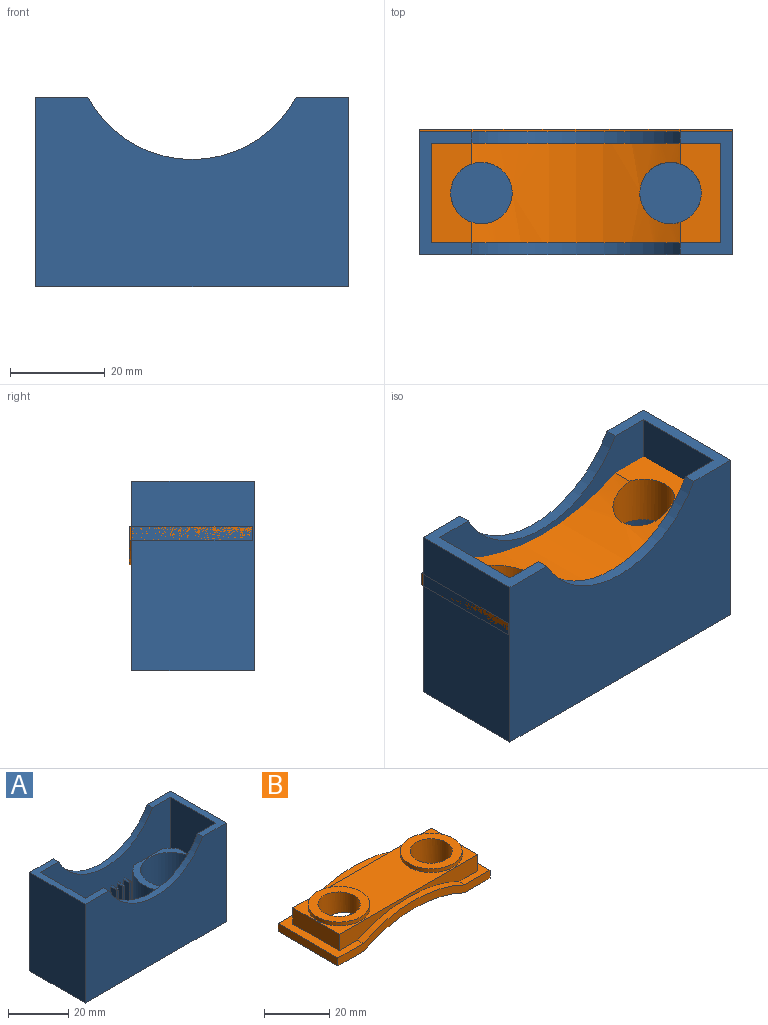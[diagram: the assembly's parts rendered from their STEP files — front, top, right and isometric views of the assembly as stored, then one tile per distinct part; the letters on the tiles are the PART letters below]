
ASSEMBLY  parts=2 mates=2
PART A: 147 faces, bbox 66x26x40 mm
  f0: cylinder r=12.5mm len=21mm, axis (0,0,-1), area 448.8mm2, adj f6,f12,f19,f141
  f1: cylinder r=12.5mm len=18mm, axis (0,0,-1), area 95.3mm2, adj f14,f19,f23,f141
  f2: cylinder r=12.5mm len=18mm, axis (0,0,-1), area 95.3mm2, adj f12,f14,f24,f141
  f3: cylinder r=12.5mm len=18mm, axis (0,0,-1), area 95.3mm2, adj f12,f18,f26,f142
  f4: cylinder r=12.5mm len=18mm, axis (0,0,-1), area 95.3mm2, adj f18,f19,f25,f142
  f5: cylinder r=12.5mm len=21mm, axis (0,0,-1), area 448.8mm2, adj f11,f12,f19,f142
  f6: plane 21x6.72mm, normal (0,0,1), area 51mm2, adj f0,f12,f19,f37,f39,f40,f41,f42
  f7: plane 21x2mm, normal (0,0,1), area 42mm2, adj f12,f19,f35,f38
  f8: plane 21x2mm, normal (0,0,1), area 42mm2, adj f12,f19,f32,f33
  f9: plane 21x2mm, normal (0,0,1), area 42mm2, adj f12,f19,f29,f31
  f10: plane 21x2mm, normal (0,0,1), area 42mm2, adj f12,f19,f30,f36
  f11: plane 21x6.72mm, normal (0,0,1), area 51mm2, adj f5,f12,f19,f34,f43,f44,f45,f46
  f12: plane 61x37mm, normal (0,1,0), area 1254.2mm2, adj f0,f2,f3,f5,f6,f7,f8,f9
  f13: plane 26x11mm, normal (0,0,1), area 107.5mm2, adj f12,f15,f16,f17,f18,f19,f27,f28
  f14: plane 37x21mm, normal (1,0,0), area 532.8mm2, adj f1,f2,f12,f19,f21,f23,f24,f141
  f15: plane 66x40mm, normal (0,-1,0), area 2228.8mm2, adj f13,f16,f20,f21,f22,f28
  f16: plane 40x26mm, normal (1,0,0), area 1040mm2, adj f13,f15,f17,f22
  f17: plane 66x40mm, normal (0,1,0), area 2228.8mm2, adj f13,f16,f20,f21,f22,f27
  f18: plane 37x21mm, normal (-1,0,0), area 532.8mm2, adj f3,f4,f12,f13,f19,f25,f26,f142
  f19: plane 61x37mm, normal (0,-1,0), area 1254.2mm2, adj f0,f1,f4,f5,f6,f7,f8,f9
  f20: plane 40x26mm, normal (-1,0,0), area 1040mm2, adj f15,f17,f21,f22
  f21: plane 26x11mm, normal (0,0,1), area 107.5mm2, adj f12,f14,f15,f17,f19,f20,f27,f28
  f22: plane 66x26mm, normal (0,0,-1), area 1716mm2, adj f15,f16,f17,f20
  f23: plane 3.72x3.72mm, normal (0,0,1), area 5.9mm2, adj f1,f14,f19
  f24: plane 3.72x3.72mm, normal (0,0,1), area 5.9mm2, adj f2,f12,f14
  f25: plane 3.72x3.72mm, normal (0,0,1), area 5.9mm2, adj f4,f18,f19
  f26: plane 3.72x3.72mm, normal (0,0,1), area 5.9mm2, adj f3,f12,f18
  f27: cylinder r=25mm len=44mm, axis (0,-1,0), area 134.5mm2, adj f13,f17,f19,f21
  f28: cylinder r=25mm len=44mm, axis (0,-1,0), area 134.5mm2, adj f12,f13,f15,f21
  f29: plane 21x14.5mm, normal (1,0,0), area 144.5mm2, adj f9,f12,f19,f63,f65,f66,f98,f127
  f30: plane 21x14.5mm, normal (-1,0,0), area 144.5mm2, adj f10,f12,f19,f64,f67,f68,f97,f125
  f31: plane 21x14.5mm, normal (-1,0,0), area 144.5mm2, adj f9,f12,f19,f57,f58,f60,f93,f121
  f32: plane 21x14.5mm, normal (1,0,0), area 144.5mm2, adj f8,f12,f19,f59,f61,f62,f94,f123
  f33: plane 21x14.5mm, normal (-1,0,0), area 144.5mm2, adj f8,f12,f19,f51,f52,f54,f89,f117
  f34: plane 21x14.5mm, normal (1,0,0), area 144.5mm2, adj f11,f12,f19,f53,f55,f56,f90,f119
  f35: plane 21x14.5mm, normal (-1,0,0), area 144.5mm2, adj f7,f12,f19,f69,f70,f72,f101,f138
  f36: plane 21x14.5mm, normal (1,0,0), area 144.5mm2, adj f10,f12,f19,f71,f73,f74,f102,f137
  f37: plane 21x14.5mm, normal (-1,0,0), area 144.5mm2, adj f6,f12,f19,f76,f79,f80,f105,f134
  f38: plane 21x14.5mm, normal (1,0,0), area 144.5mm2, adj f7,f12,f19,f75,f77,f78,f106,f133
  f39: plane 14.5x2.5mm, normal (1,0,0), area 36.3mm2, adj f6,f19,f84,f129
  f40: plane 14.5x2.5mm, normal (-1,0,0), area 36.3mm2, adj f6,f19,f83,f130
  f41: plane 14.5x2.5mm, normal (-1,0,0), area 36.3mm2, adj f6,f12,f48,f109
  f42: plane 14.5x2.5mm, normal (1,0,0), area 36.3mm2, adj f6,f12,f47,f110
  f43: plane 14.5x2.5mm, normal (-1,0,0), area 36.3mm2, adj f11,f19,f81,f113
  f44: plane 14.5x2.5mm, normal (1,0,0), area 36.3mm2, adj f11,f19,f82,f115
  f45: plane 14.5x2.5mm, normal (-1,0,0), area 36.3mm2, adj f11,f12,f50,f85
  f46: plane 14.5x2.5mm, normal (1,0,0), area 36.3mm2, adj f11,f12,f49,f86
  f47: plane 14.5x0.5mm, normal (0.71,0.71,0), area 10.3mm2, adj f6,f42,f48,f112
  f48: plane 14.5x0.5mm, normal (-0.71,0.71,0), area 10.3mm2, adj f6,f41,f47,f111
  f49: plane 14.5x0.5mm, normal (0.71,0.71,0), area 10.3mm2, adj f11,f46,f50,f88
  f50: plane 14.5x0.5mm, normal (-0.71,0.71,0), area 10.3mm2, adj f11,f45,f49,f87
  f51: plane 10x0.5mm, normal (-0.71,-0.71,0), area 6.9mm2, adj f33,f52,f53,f118
  f52: plane 16x0.5mm, normal (-0.71,0,0.71), area 11mm2, adj f33,f51,f54,f55
  f53: plane 10x0.5mm, normal (0.71,-0.71,0), area 6.9mm2, adj f34,f51,f55,f120
  f54: plane 10x0.5mm, normal (-0.71,0.71,0), area 6.9mm2, adj f33,f52,f56,f91
  f55: plane 16x0.5mm, normal (0.71,0,0.71), area 11mm2, adj f34,f52,f53,f56
  f56: plane 10x0.5mm, normal (0.71,0.71,0), area 6.9mm2, adj f34,f54,f55,f92
  f57: plane 10x0.5mm, normal (-0.71,-0.71,0), area 6.9mm2, adj f31,f58,f59,f122
  f58: plane 16x0.5mm, normal (-0.71,0,0.71), area 11mm2, adj f31,f57,f60,f61
  f59: plane 10x0.5mm, normal (0.71,-0.71,0), area 6.9mm2, adj f32,f57,f61,f124
  f60: plane 10x0.5mm, normal (-0.71,0.71,0), area 6.9mm2, adj f31,f58,f62,f95
  f61: plane 16x0.5mm, normal (0.71,0,0.71), area 11mm2, adj f32,f58,f59,f62
  f62: plane 10x0.5mm, normal (0.71,0.71,0), area 6.9mm2, adj f32,f60,f61,f96
  f63: plane 10x0.5mm, normal (0.71,-0.71,0), area 6.9mm2, adj f29,f64,f65,f128
  f64: plane 10x0.5mm, normal (-0.71,-0.71,0), area 6.9mm2, adj f30,f63,f67,f126
  f65: plane 16x0.5mm, normal (0.71,0,0.71), area 11mm2, adj f29,f63,f66,f67
  f66: plane 10x0.5mm, normal (0.71,0.71,0), area 6.9mm2, adj f29,f65,f68,f100
  f67: plane 16x0.5mm, normal (-0.71,0,0.71), area 11mm2, adj f30,f64,f65,f68
  f68: plane 10x0.5mm, normal (-0.71,0.71,0), area 6.9mm2, adj f30,f66,f67,f99
  f69: plane 10x0.5mm, normal (-0.71,-0.71,0), area 6.9mm2, adj f35,f70,f71,f140
  f70: plane 16x0.5mm, normal (-0.71,0,0.71), area 11mm2, adj f35,f69,f72,f73
  f71: plane 10x0.5mm, normal (0.71,-0.71,0), area 6.9mm2, adj f36,f69,f73,f139
  f72: plane 10x0.5mm, normal (-0.71,0.71,0), area 6.9mm2, adj f35,f70,f74,f103
  f73: plane 16x0.5mm, normal (0.71,0,0.71), area 11mm2, adj f36,f70,f71,f74
  f74: plane 10x0.5mm, normal (0.71,0.71,0), area 6.9mm2, adj f36,f72,f73,f104
  f75: plane 10x0.5mm, normal (0.71,-0.71,0), area 6.9mm2, adj f38,f76,f77,f135
  f76: plane 10x0.5mm, normal (-0.71,-0.71,0), area 6.9mm2, adj f37,f75,f79,f136
  f77: plane 16x0.5mm, normal (0.71,0,0.71), area 11mm2, adj f38,f75,f78,f79
  f78: plane 10x0.5mm, normal (0.71,0.71,0), area 6.9mm2, adj f38,f77,f80,f108
  f79: plane 16x0.5mm, normal (-0.71,0,0.71), area 11mm2, adj f37,f76,f77,f80
  f80: plane 10x0.5mm, normal (-0.71,0.71,0), area 6.9mm2, adj f37,f78,f79,f107
  f81: plane 14.5x0.5mm, normal (-0.71,-0.71,0), area 10.3mm2, adj f11,f43,f82,f114
  f82: plane 14.5x0.5mm, normal (0.71,-0.71,0), area 10.3mm2, adj f11,f44,f81,f116
  f83: plane 14.5x0.5mm, normal (-0.71,-0.71,0), area 10.3mm2, adj f6,f40,f84,f132
  f84: plane 14.5x0.5mm, normal (0.71,-0.71,0), area 10.3mm2, adj f6,f39,f83,f131
  f85: plane 2.5x0.5mm, normal (-0.71,0,0.71), area 1.7mm2, adj f12,f45,f86,f87
  f86: plane 2.5x0.5mm, normal (0.71,0,0.71), area 1.7mm2, adj f12,f46,f85,f88
  f87: plane 0.71x0.5mm, normal (-0.5,0.5,0.71), area 0.2mm2, adj f50,f85,f88
  f88: plane 0.71x0.5mm, normal (0.5,0.5,0.71), area 0.3mm2, adj f49,f86,f87
  f89: plane 2.5x0.5mm, normal (-0.71,0,0.71), area 1.7mm2, adj f12,f33,f90,f91
  f90: plane 2.5x0.5mm, normal (0.71,0,0.71), area 1.7mm2, adj f12,f34,f89,f92
  f91: plane 0.71x0.5mm, normal (-0.5,0.5,0.71), area 0.2mm2, adj f54,f89,f92
  f92: plane 0.71x0.5mm, normal (0.5,0.5,0.71), area 0.2mm2, adj f56,f90,f91
  f93: plane 2.5x0.5mm, normal (-0.71,0,0.71), area 1.7mm2, adj f12,f31,f94,f95
  f94: plane 2.5x0.5mm, normal (0.71,0,0.71), area 1.7mm2, adj f12,f32,f93,f96
  f95: plane 0.71x0.5mm, normal (-0.5,0.5,0.71), area 0.2mm2, adj f60,f93,f96
  f96: plane 0.71x0.5mm, normal (0.5,0.5,0.71), area 0.2mm2, adj f62,f94,f95
  f97: plane 2.5x0.5mm, normal (-0.71,0,0.71), area 1.7mm2, adj f12,f30,f98,f99
  f98: plane 2.5x0.5mm, normal (0.71,0,0.71), area 1.7mm2, adj f12,f29,f97,f100
  f99: plane 0.71x0.5mm, normal (-0.5,0.5,0.71), area 0.2mm2, adj f68,f97,f100
  f100: plane 0.71x0.5mm, normal (0.5,0.5,0.71), area 0.2mm2, adj f66,f98,f99
  f101: plane 2.5x0.5mm, normal (-0.71,0,0.71), area 1.7mm2, adj f12,f35,f102,f103
  f102: plane 2.5x0.5mm, normal (0.71,0,0.71), area 1.7mm2, adj f12,f36,f101,f104
  f103: plane 0.71x0.5mm, normal (-0.5,0.5,0.71), area 0.3mm2, adj f72,f101,f104
  f104: plane 0.71x0.5mm, normal (0.5,0.5,0.71), area 0.2mm2, adj f74,f102,f103
  f105: plane 2.5x0.5mm, normal (-0.71,0,0.71), area 1.7mm2, adj f12,f37,f106,f107
  f106: plane 2.5x0.5mm, normal (0.71,0,0.71), area 1.7mm2, adj f12,f38,f105,f108
  f107: plane 0.71x0.5mm, normal (-0.5,0.5,0.71), area 0.2mm2, adj f80,f105,f108
  f108: plane 0.71x0.5mm, normal (0.5,0.5,0.71), area 0.2mm2, adj f78,f106,f107
  f109: plane 2.5x0.5mm, normal (-0.71,0,0.71), area 1.7mm2, adj f12,f41,f110,f111
  f110: plane 2.5x0.5mm, normal (0.71,0,0.71), area 1.7mm2, adj f12,f42,f109,f112
  f111: plane 0.71x0.5mm, normal (-0.5,0.5,0.71), area 0.2mm2, adj f48,f109,f112
  f112: plane 0.71x0.5mm, normal (0.5,0.5,0.71), area 0.3mm2, adj f47,f110,f111
  f113: plane 2.5x0.5mm, normal (-0.71,0,0.71), area 1.7mm2, adj f19,f43,f114,f115
  f114: plane 0.71x0.5mm, normal (-0.5,-0.5,0.71), area 0.2mm2, adj f81,f113,f116
  f115: plane 2.5x0.5mm, normal (0.71,0,0.71), area 1.7mm2, adj f19,f44,f113,f116
  f116: plane 0.71x0.5mm, normal (0.5,-0.5,0.71), area 0.3mm2, adj f82,f114,f115
  f117: plane 2.5x0.5mm, normal (-0.71,0,0.71), area 1.7mm2, adj f19,f33,f118,f119
  f118: plane 0.71x0.5mm, normal (-0.5,-0.5,0.71), area 0.2mm2, adj f51,f117,f120
  f119: plane 2.5x0.5mm, normal (0.71,0,0.71), area 1.7mm2, adj f19,f34,f117,f120
  f120: plane 0.71x0.5mm, normal (0.5,-0.5,0.71), area 0.3mm2, adj f53,f118,f119
  f121: plane 2.5x0.5mm, normal (-0.71,0,0.71), area 1.7mm2, adj f19,f31,f122,f123
  f122: plane 0.71x0.5mm, normal (-0.5,-0.5,0.71), area 0.2mm2, adj f57,f121,f124
  f123: plane 2.5x0.5mm, normal (0.71,0,0.71), area 1.7mm2, adj f19,f32,f121,f124
  f124: plane 0.71x0.5mm, normal (0.5,-0.5,0.71), area 0.2mm2, adj f59,f122,f123
  f125: plane 2.5x0.5mm, normal (-0.71,0,0.71), area 1.7mm2, adj f19,f30,f126,f127
  f126: plane 0.71x0.5mm, normal (-0.5,-0.5,0.71), area 0.2mm2, adj f64,f125,f128
  f127: plane 2.5x0.5mm, normal (0.71,0,0.71), area 1.7mm2, adj f19,f29,f125,f128
  f128: plane 0.71x0.5mm, normal (0.5,-0.5,0.71), area 0.3mm2, adj f63,f126,f127
  f129: plane 2.5x0.5mm, normal (0.71,0,0.71), area 1.7mm2, adj f19,f39,f130,f131
  f130: plane 2.5x0.5mm, normal (-0.71,0,0.71), area 1.7mm2, adj f19,f40,f129,f132
  f131: plane 0.71x0.5mm, normal (0.5,-0.5,0.71), area 0.3mm2, adj f84,f129,f132
  f132: plane 0.71x0.5mm, normal (-0.5,-0.5,0.71), area 0.2mm2, adj f83,f130,f131
  f133: plane 2.5x0.5mm, normal (0.71,0,0.71), area 1.7mm2, adj f19,f38,f134,f135
  f134: plane 2.5x0.5mm, normal (-0.71,0,0.71), area 1.7mm2, adj f19,f37,f133,f136
  f135: plane 0.71x0.5mm, normal (0.5,-0.5,0.71), area 0.3mm2, adj f75,f133,f136
  f136: plane 0.71x0.5mm, normal (-0.5,-0.5,0.71), area 0.2mm2, adj f76,f134,f135
  f137: plane 2.5x0.5mm, normal (0.71,0,0.71), area 1.7mm2, adj f19,f36,f138,f139
  f138: plane 2.5x0.5mm, normal (-0.71,0,0.71), area 1.7mm2, adj f19,f35,f137,f140
  f139: plane 0.71x0.5mm, normal (0.5,-0.5,0.71), area 0.2mm2, adj f71,f137,f140
  f140: plane 0.71x0.5mm, normal (-0.5,-0.5,0.71), area 0.2mm2, adj f69,f138,f139
  f141: plane 23x21mm, normal (0,0,1), area 121.5mm2, adj f0,f1,f2,f12,f14,f19,f144
  f142: plane 23x21mm, normal (0,0,1), area 121.5mm2, adj f3,f4,f5,f12,f18,f19,f146
  f143: plane 20x20mm, normal (0,0,1), area 314.2mm2, adj f144
  f144: cylinder r=10mm len=20mm, axis (0,0,-1), area 1131mm2, adj f141,f143
  f145: plane 20x20mm, normal (0,0,1), area 314.2mm2, adj f146
  f146: cylinder r=10mm len=20mm, axis (0,0,-1), area 1131mm2, adj f142,f145
PART B: 22 faces, bbox 66x26x10.5 mm
  f0: plane 60x6.1mm, normal (0,-1,0), area 214.8mm2, adj f1,f3,f4,f11,f12,f15
  f1: plane 20x6.1mm, normal (1,0,0), area 122mm2, adj f0,f2,f4,f12
  f2: plane 60x6.1mm, normal (0,1,0), area 214.8mm2, adj f1,f3,f4,f9,f12,f15
  f3: plane 20x6.1mm, normal (-1,0,0), area 122mm2, adj f0,f2,f4,f15
  f4: plane 60x20mm, normal (0,0,1), area 632.9mm2, adj f0,f1,f2,f3,f5,f7
  f5: cylinder r=9.5mm len=19mm, axis (0,0,-1), area 81.8mm2, adj f4,f6
  f6: plane 19x19mm, normal (0,0,1), area 150.8mm2, adj f5,f20
  f7: cylinder r=9.5mm len=19mm, axis (0,0,-1), area 81.8mm2, adj f4,f8
  f8: plane 19x19mm, normal (0,0,1), area 150.8mm2, adj f7,f21
  f9: cylinder r=50mm len=44mm, axis (0,-1,0), area 159.5mm2, adj f2,f12,f15,f16
  f10: cylinder r=50mm len=44mm, axis (0,-1,0), area 986.6mm2, adj f13,f14,f16,f17,f20,f21
  f11: cylinder r=50mm len=44mm, axis (0,-1,0), area 113.9mm2, adj f0,f12,f15,f17
  f12: plane 26x11mm, normal (0,0,1), area 126mm2, adj f0,f1,f2,f9,f11,f16,f17,f19
  f13: plane 26x11mm, normal (0,0,-1), area 245.2mm2, adj f10,f16,f17,f19,f21
  f14: plane 26x11mm, normal (0,0,-1), area 245.2mm2, adj f10,f16,f17,f18,f20
  f15: plane 26x11mm, normal (0,0,1), area 126mm2, adj f0,f2,f3,f9,f11,f16,f17,f18
  f16: plane 66x8.1mm, normal (0,1,0), area 198mm2, adj f9,f10,f12,f13,f14,f15,f18,f19
  f17: plane 66x8.1mm, normal (0,-1,0), area 198mm2, adj f10,f11,f12,f13,f14,f15,f18,f19
  f18: plane 26x3mm, normal (-1,0,0), area 78mm2, adj f14,f15,f16,f17
  f19: plane 26x3mm, normal (1,0,0), area 78mm2, adj f12,f13,f16,f17
  f20: cylinder r=6.5mm len=13mm, axis (0,0,1), area 375.3mm2, adj f6,f10,f14
  f21: cylinder r=6.5mm len=13mm, axis (0,0,1), area 375.3mm2, adj f8,f10,f13
PLACE A t=(0.96,-31.04,-4.27)mm
PLACE B rot(axis=(0,-1,0),180deg) t=(0.96,-31.04,18.1)mm
MATE fastened B.f5 <-> A.f146  axis (0,0,-1) through (20.96,-31.04,15.73)mm
MATE revolute A.f146 <-> A.f16  axis (0,0,-1) through (20.96,-31.04,16.73)mm
